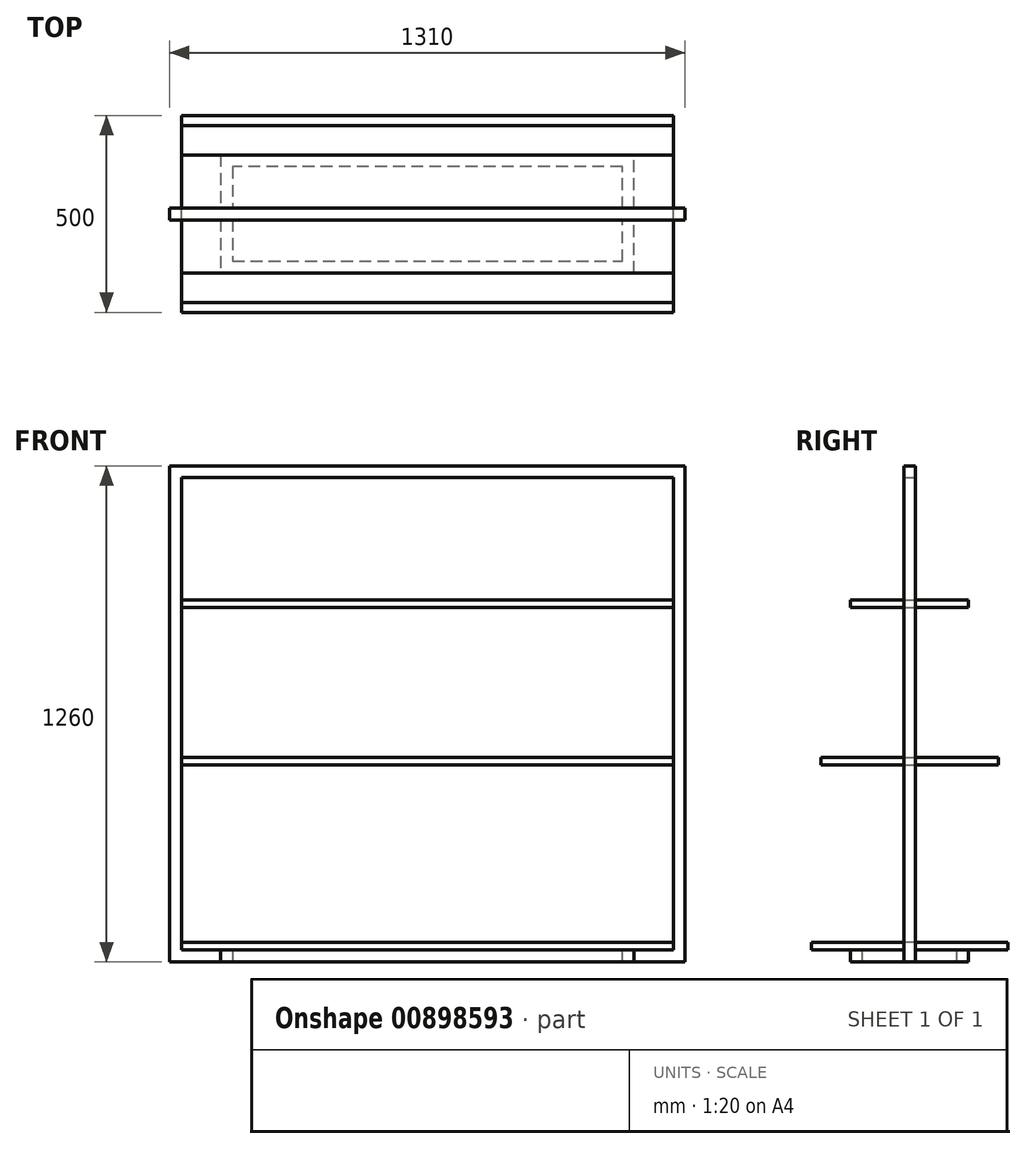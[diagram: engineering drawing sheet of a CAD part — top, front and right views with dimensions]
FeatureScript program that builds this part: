
annotation { "Feature Type Name" : "Feature", "Feature Type Description" : "" }
export const myFeature = defineFeature(function(context is Context, id is Id, definition is map)
    precondition{}
    {
        {
            var Q0;
            Q0=qCreatedBy(makeId("Top.planeOp"),FACE);
            var sketch = newSketch(context, id + "F0", { "sketchPlane" : qUnion([Q0])});
            skLineSegment(sketch, "E0.bottom", {"start": v(-625, 250) * mm, "end": v(625, 250) * mm});
            skLineSegment(sketch, "E0.top", {"start": v(-625, -250) * mm, "end": v(625, -250) * mm});
            skLineSegment(sketch, "E0.left", {"start": v(-625, 250) * mm, "end": v(-625, -250) * mm});
            skLineSegment(sketch, "E0.right", {"start": v(625, 250) * mm, "end": v(625, -250) * mm});
            skLineSegment(sketch, "E1", {"start": v(-625, 250) * mm, "end": v(625, -250) * mm, "construction": true});
            skSolve(sketch);
        }
        {
            var Q0;
            Q0=qSketchRegion(id+"F0",true);
            extrude(context, id + "F1", {"entities" : qUnion([Q0]), "depth" : 20 * mm, "offsetDistance" : 25 * mm});
        }
        {
            var Q0;
            Q0=qCreatedBy(makeId("Front.planeOp"),FACE);
            var sketch = newSketch(context, id + "F2", { "sketchPlane" : qUnion([Q0])});
            skLineSegment(sketch, "E2", {"start": v(625, 0) * mm, "end": v(625, 1200) * mm});
            skLineSegment(sketch, "E3", {"start": v(625, 1200) * mm, "end": v(-625, 1200) * mm});
            skLineSegment(sketch, "E4", {"start": v(-625, 1200) * mm, "end": v(-625, 0) * mm});
            skLineSegment(sketch, "E5", {"start": v(-625, 0) * mm, "end": v(625, 0) * mm});
            skLineSegment(sketch, "E6.0", {"start": v(655, 1230) * mm, "end": v(-655, 1230) * mm});
            skLineSegment(sketch, "E6.1", {"start": v(655, -30) * mm, "end": v(655, 1230) * mm});
            skLineSegment(sketch, "E6.2", {"start": v(-655, -30) * mm, "end": v(655, -30) * mm});
            skLineSegment(sketch, "E6.3", {"start": v(-655, 1230) * mm, "end": v(-655, -30) * mm});
            skSolve(sketch);
        }
        {
            var Q0;
            Q0=qSketchRegion(id+"F2",true);
            extrude(context, id + "F3", {"entities" : qUnion([Q0]), "endBound" : BoundingType.SYMMETRIC, "depth" : 30 * mm, "offsetDistance" : 25 * mm});
        }
        {
            var Q0;
            Q0=makeQuery(id+"F1.opExtrude","CAP_FACE",FACE,{"disambiguationData":[OSD([sQuery(id+"F0.wireOp",EDGE,"E0.bottom"),sQuery(id+"F0.wireOp",EDGE,"E0.top"),sQuery(id+"F0.wireOp",EDGE,"E0.left"),sQuery(id+"F0.wireOp",EDGE,"E0.right")])],"isStart":true});
            var sketch = newSketch(context, id + "F4", { "sketchPlane" : qUnion([Q0])});
            skLineSegment(sketch, "E7", {"start": v(525, 150) * mm, "end": v(525, -150) * mm});
            skLineSegment(sketch, "E8", {"start": v(525, -150) * mm, "end": v(-525, -150) * mm});
            skLineSegment(sketch, "E9", {"start": v(-525, -150) * mm, "end": v(-525, 150) * mm});
            skLineSegment(sketch, "E10", {"start": v(-525, 150) * mm, "end": v(525, 150) * mm});
            skLineSegment(sketch, "E11.0", {"start": v(-495, 120) * mm, "end": v(495, 120) * mm});
            skLineSegment(sketch, "E11.1", {"start": v(-495, -120) * mm, "end": v(-495, 120) * mm});
            skLineSegment(sketch, "E11.2", {"start": v(495, -120) * mm, "end": v(-495, -120) * mm});
            skLineSegment(sketch, "E11.3", {"start": v(495, 120) * mm, "end": v(495, -120) * mm});
            skSolve(sketch);
        }
        {
            var Q0;
            Q0=qSketchRegion(id+"F4",true);
            extrude(context, id + "F5", {"entities" : qUnion([Q0]), "operationType" : NewBodyOperationType.ADD, "depth" : 30 * mm, "offsetDistance" : 25 * mm});
        }
        {
            var Q0;
            Q0=qCreatedBy(makeId("Front.planeOp"),FACE);
            var sketch = newSketch(context, id + "F6", { "sketchPlane" : qUnion([Q0])});
            skLineSegment(sketch, "E12.bottom", {"start": v(-625, 890) * mm, "end": v(625, 890) * mm});
            skLineSegment(sketch, "E12.top", {"start": v(-625, 870) * mm, "end": v(625, 870) * mm});
            skLineSegment(sketch, "E12.left", {"start": v(-625, 890) * mm, "end": v(-625, 870) * mm});
            skLineSegment(sketch, "E12.right", {"start": v(625, 890) * mm, "end": v(625, 870) * mm});
            skSolve(sketch);
        }
        {
            var Q0;
            Q0 = qSketchRegion(id + "F6", true);
            extrude(context, id + "F7", {"entities" : qUnion([Q0]), "endBound" : BoundingType.SYMMETRIC, "depth" : 300 * mm, "offsetDistance" : 25 * mm});
        }
        {
            var Q0;
            Q0=qCreatedBy(makeId("Front.planeOp"),FACE);
            var sketch = newSketch(context, id + "F8", { "sketchPlane" : qUnion([Q0])});
            skLineSegment(sketch, "E13.bottom", {"start": v(-625, 490) * mm, "end": v(625, 490) * mm});
            skLineSegment(sketch, "E13.top", {"start": v(-625, 470) * mm, "end": v(625, 470) * mm});
            skLineSegment(sketch, "E13.left", {"start": v(-625, 490) * mm, "end": v(-625, 470) * mm});
            skLineSegment(sketch, "E13.right", {"start": v(625, 490) * mm, "end": v(625, 470) * mm});
            skSolve(sketch);
        }
        {
            var Q0;
            Q0 = qSketchRegion(id + "F8", true);
            extrude(context, id + "F9", {"entities" : qUnion([Q0]), "endBound" : BoundingType.SYMMETRIC, "depth" : 450 * mm, "offsetDistance" : 25 * mm});
        }
    });
